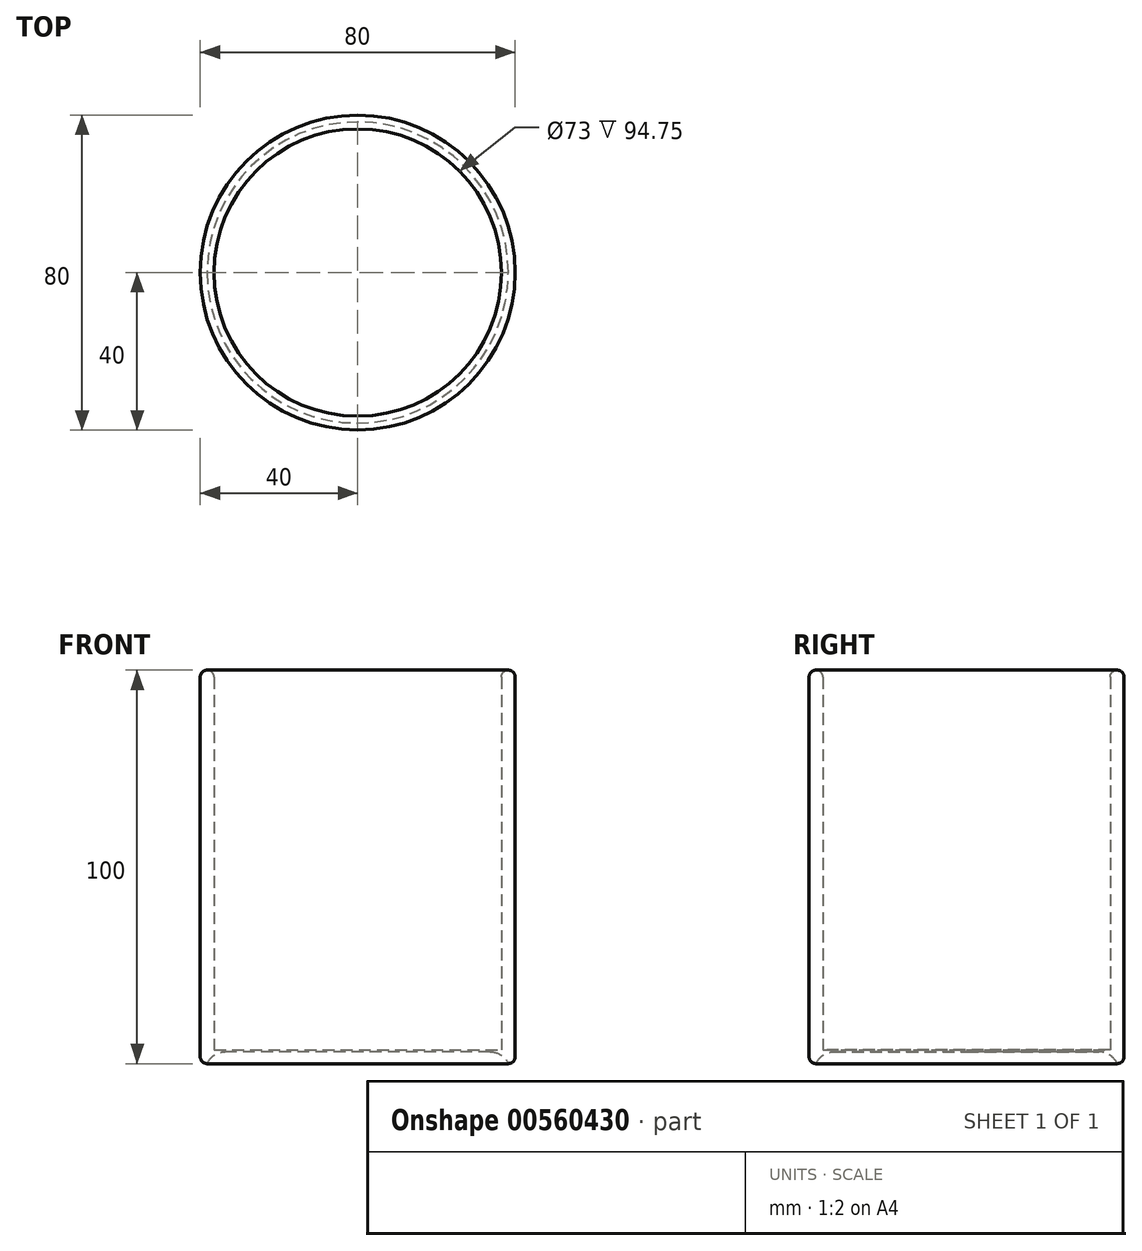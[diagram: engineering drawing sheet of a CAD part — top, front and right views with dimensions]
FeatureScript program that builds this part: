
annotation { "Feature Type Name" : "Feature", "Feature Type Description" : "" }
export const myFeature = defineFeature(function(context is Context, id is Id, definition is map)
    precondition{}
    {
        {
            var Q0;
            Q0=qCreatedBy(makeId("Front.planeOp"),FACE);
            var sketch = newSketch(context, id + "F0", { "sketchPlane" : qUnion([Q0])});
            skLineSegment(sketch, "E0.bottom", {"start": v(0, 0) * mm, "end": v(40, 0) * mm});
            skLineSegment(sketch, "E0.top", {"start": v(0, 100) * mm, "end": v(40, 100) * mm});
            skLineSegment(sketch, "E0.left", {"start": v(0, 0) * mm, "end": v(0, 100) * mm});
            skLineSegment(sketch, "E0.right", {"start": v(40, 0) * mm, "end": v(40, 100) * mm});
            skFitSpline(sketch, "E1", {"points": [v(30.42, 80.8) * mm, v(68.02, 80.8) * mm, v(81.11, 60.93) * mm, v(79.85, 27.56) * mm, v(55.34, 10.66) * mm, v(29.15, 10.24) * mm], "startDerivative": vector(192.02, 28.39) * mm, "endDerivative": vector(-137.66, 13.74) * mm});
            skFitSpline(sketch, "E2.0", {"points": [v(31.73, 71.89) * mm, v(33.73, 72.18) * mm, v(37.7, 72.77) * mm, v(43.4, 73.52) * mm, v(48.77, 74.06) * mm, v(53.68, 74.3) * mm, v(57.25, 74.19) * mm, v(59.71, 73.9) * mm, v(61.34, 73.61) * mm, v(62.72, 73.24) * mm, v(63.67, 72.89) * mm, v(64.3, 72.6) * mm, v(64.9, 72.28) * mm, v(65.58, 71.83) * mm, v(66.37, 71.19) * mm, v(67.14, 70.41) * mm, v(67.9, 69.48) * mm, v(68.89, 68.01) * mm, v(69.85, 66.18) * mm, v(70.75, 64) * mm, v(71.39, 62.2) * mm, v(71.89, 60.57) * mm, v(72.27, 59.2) * mm, v(72.63, 57.8) * mm, v(73.06, 55.99) * mm, v(73.5, 53.78) * mm, v(73.86, 51.55) * mm, v(74.24, 48.57) * mm, v(74.48, 44.87) * mm, v(74.35, 40.66) * mm, v(73.88, 37.46) * mm, v(73.29, 35.15) * mm, v(72.74, 33.57) * mm, v(72.2, 32.36) * mm, v(71.74, 31.48) * mm, v(71.22, 30.6) * mm, v(70.48, 29.53) * mm, v(69.1, 27.86) * mm, v(67.02, 25.88) * mm, v(64, 23.74) * mm, v(60.62, 21.9) * mm, v(57.6, 20.68) * mm, v(55.15, 19.9) * mm, v(53.32, 19.41) * mm, v(51.5, 19.03) * mm, v(49.08, 18.64) * mm, v(46.02, 18.35) * mm, v(42.24, 18.29) * mm, v(37.04, 18.5) * mm, v(32.91, 18.9) * mm, v(30.04, 19.2) * mm]});
            skLineSegment(sketch, "E3", {"start": v(30.42, 80.8) * mm, "end": v(31.73, 71.89) * mm});
            skLineSegment(sketch, "E4", {"start": v(30.04, 19.2) * mm, "end": v(29.15, 10.24) * mm});
            skSolve(sketch);
        }
        {
            var Q0;
            {var subQ10=sQuery(id+"F0.wireOp",EDGE,"E0.bottom");Q0=makeQuery(id+"F0.imprint","IMPRINT",FACE,{"disambiguationData":[TD([[makeQuery(id+"F0.imprint","IMPRINT",EDGE,{"derivedFrom":subQ10}),1.0]])]});}
            var Q1;
            {var subQ5=sQuery(id+"F0.wireOp",EDGE,"E3");Q1=makeQuery(id+"F0.imprint","IMPRINT",FACE,{"disambiguationData":[TD([[makeQuery(id+"F0.imprint","IMPRINT",EDGE,{"derivedFrom":subQ5}),1.0]])]});}
            var Q2;
            {var subQ5=sQuery(id+"F0.wireOp",EDGE,"E4");Q2=makeQuery(id+"F0.imprint","IMPRINT",FACE,{"disambiguationData":[TD([[makeQuery(id+"F0.imprint","IMPRINT",EDGE,{"derivedFrom":subQ5}),1.0]])]});}
            var Q3;
            Q3=sQuery(id+"F0.wireOp",EDGE,"E0.left");
            revolve(context, id + "F1", {"entities" : qUnion([Q0, Q1, Q2]), "axis" : qUnion([Q3]), "revolveType" : RevolveType.FULL});
        }
        {
            var Q0;
            Q0=makeQuery(id+"F1.opRevolve","SWEPT_FACE",FACE,{"disambiguationData":[OSD([sQuery(id+"F0.wireOp",EDGE,"E0.top")])]});
            shell(context, id + "F2", {"entities" : qUnion([Q0]), "thickness" : 3.5 * mm});
        }
        {
            var Q0;
            Q0=makeQuery(id+"F1.opRevolve","SWEPT_EDGE",EDGE,{"disambiguationData":[OSD([sQuery(id+"F0.wireOp",EDGE,"E0.top"),sQuery(id+"F0.wireOp",EDGE,"E0.right")])]});
            var Q1;
            Q1=makeQuery(id+"F2.opShell","OFFSET_EDGE",EDGE,{"disambiguationData":[OSD([sQuery(id+"F0.wireOp",EDGE,"E0.top"),sQuery(id+"F0.wireOp",EDGE,"E0.right")])]});
            fillet(context, id + "F3", {"entities" : qUnion([Q0, Q1]), "radius" : 1.75 * mm, "tangentPropagation" : true, "allowEdgeOverflow" : false});
        }
        {
            var Q0;
            Q0=qCreatedBy(makeId("Top.planeOp"),FACE);
            var sketch = newSketch(context, id + "F4", { "sketchPlane" : qUnion([Q0])});
            skCircle(sketch, "E5", {"center": v(0, 0) * mm, "radius": 38.25 * mm});
            skSolve(sketch);
        }
        {
            var Q0;
            Q0=makeQuery(id+"F4.imprint","IMPRINT",FACE,{"disambiguationData":[TD([[makeQuery(id+"F4.imprint","IMPRINT",EDGE,{"derivedFrom":sQuery(id+"F4.wireOp",EDGE,"E5")}),1.0]])]});
            extrude(context, id + "F5", {"entities" : qUnion([Q0]), "operationType" : NewBodyOperationType.REMOVE, "depth" : 3 * mm, "offsetDistance" : 25 * mm});
        }
        {
            var Q0;
            Q0=makeQuery(id+"F1.opRevolve","SWEPT_EDGE",EDGE,{"disambiguationData":[OSD([sQuery(id+"F0.wireOp",EDGE,"E0.bottom"),sQuery(id+"F0.wireOp",EDGE,"E0.right")])]});
            fillet(context, id + "F6", {"entities" : qUnion([Q0]), "radius" : 1.75 * mm, "tangentPropagation" : true, "allowEdgeOverflow" : false});
        }
        {
            var Q0;
            Q0=makeQuery(id+"F5.boolean.opBoolean","COPY",EDGE,{"derivedFrom":makeQuery(id+"F5.opExtrude","CAP_EDGE",EDGE,{"disambiguationData":[OSD([sQuery(id+"F4.wireOp",EDGE,"E5")])],"isStart":false})});
            fillet(context, id + "F7", {"entities" : qUnion([Q0]), "radius" : 5 * mm, "tangentPropagation" : true, "allowEdgeOverflow" : false});
        }
    });
